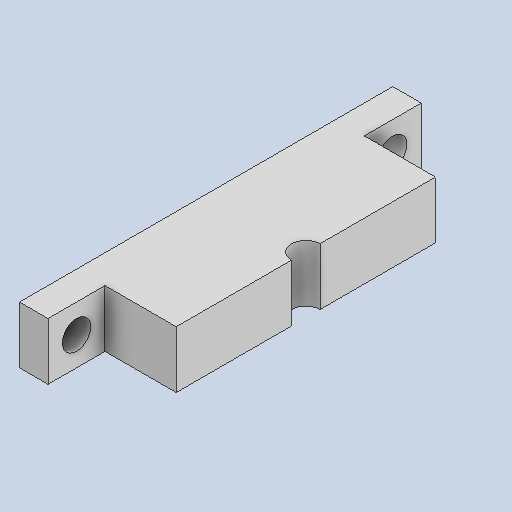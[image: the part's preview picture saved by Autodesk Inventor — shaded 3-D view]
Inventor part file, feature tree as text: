
AUTODESK INVENTOR PART (.ipt)
format: ipt  version: 2023 (Build 270158000, 158)  size: 156,672 bytes
history: native  units: mm
features: extrude x6, sketch x5
ambient origin geometry x8: Origin, YZ Plane, XZ Plane, XY Plane, X Axis, Y Axis, Z Axis, Center Point
bodies: Solid1 (feature_tree)
feature tree (11):
  sketch  "Sketch1"  dims[d0=10.0mm d1=0.0mm d2=5.0mm d3=0.0mm]
  extrude  "Extrusion1"  Depth=5.0mm TaperAngle=0.0deg
  extrude  "Extrusion2"  Depth=10.0mm TaperAngle=0.0deg
  extrude  "Extrusion4"  TaperAngle=0.0deg  [1 undecoded]
  extrude  "Extrusion5"  TaperAngle=0.0deg  [1 undecoded]
  extrude  "Extrusion6"  [1 undecoded]
  extrude  "Extrusion7"  [1 undecoded]
  sketch  "Sketch2"  dims[d4=15.0mm d7=10.0mm d8=0.0mm]
  sketch  "Sketch3"  dims[d9=5.0mm d10=0.0mm d11=0.0mm]
  sketch  "Sketch4"  dims[d12=10.0mm d13=0.0mm d14=0.0mm d15=0.0mm]
  sketch  "Sketch5"
note: 4 required parameter values undecoded (feature->parameter linkage not recoverable at this tier; creation-order binding heuristic only, values carry confidence <= 0.55)
